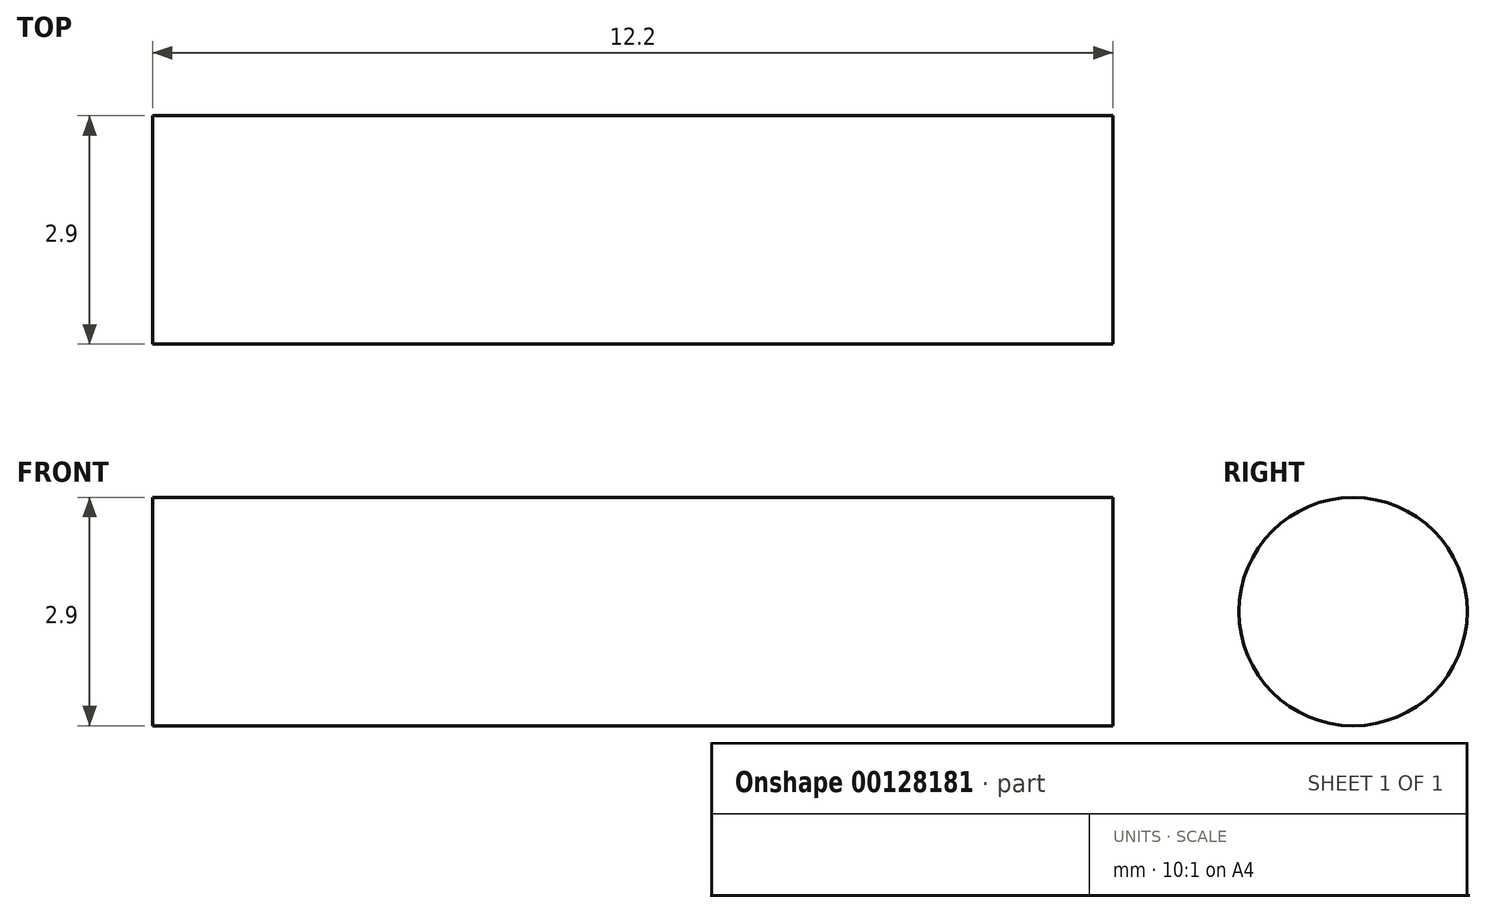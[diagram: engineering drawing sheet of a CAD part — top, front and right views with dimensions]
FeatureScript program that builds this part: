
annotation { "Feature Type Name" : "Feature", "Feature Type Description" : "" }
export const myFeature = defineFeature(function(context is Context, id is Id, definition is map)
    precondition{}
    {
        {
            var Q0;
            Q0=qCreatedBy(makeId("Front.planeOp"),FACE);
            var sketch = newSketch(context, id + "F0", { "sketchPlane" : qUnion([Q0])});
            skLineSegment(sketch, "E0", {"start": v(-6.1, 0) * mm, "end": v(6.1, 0) * mm});
            skLineSegment(sketch, "E1", {"start": v(6.1, 0) * mm, "end": v(6.1, 1.45) * mm});
            skLineSegment(sketch, "E2", {"start": v(-6.1, 0) * mm, "end": v(-6.1, 1.45) * mm});
            skLineSegment(sketch, "E3", {"start": v(-6.1, 1.45) * mm, "end": v(6.1, 1.45) * mm});
            skSolve(sketch);
        }
        {
            var Q0;
            Q0=makeQuery(id+"F0.imprint","IMPRINT",FACE,{"disambiguationData":[TD([[makeQuery(id+"F0.imprint","IMPRINT",EDGE,{"derivedFrom":sQuery(id+"F0.wireOp",EDGE,"E0")}),1.0]])]});
            var Q1;
            Q1=sQuery(id+"F0.wireOp",EDGE,"E0");
            revolve(context, id + "F1", {"entities" : qUnion([Q0]), "axis" : qUnion([Q1]), "revolveType" : RevolveType.FULL});
        }
    });
